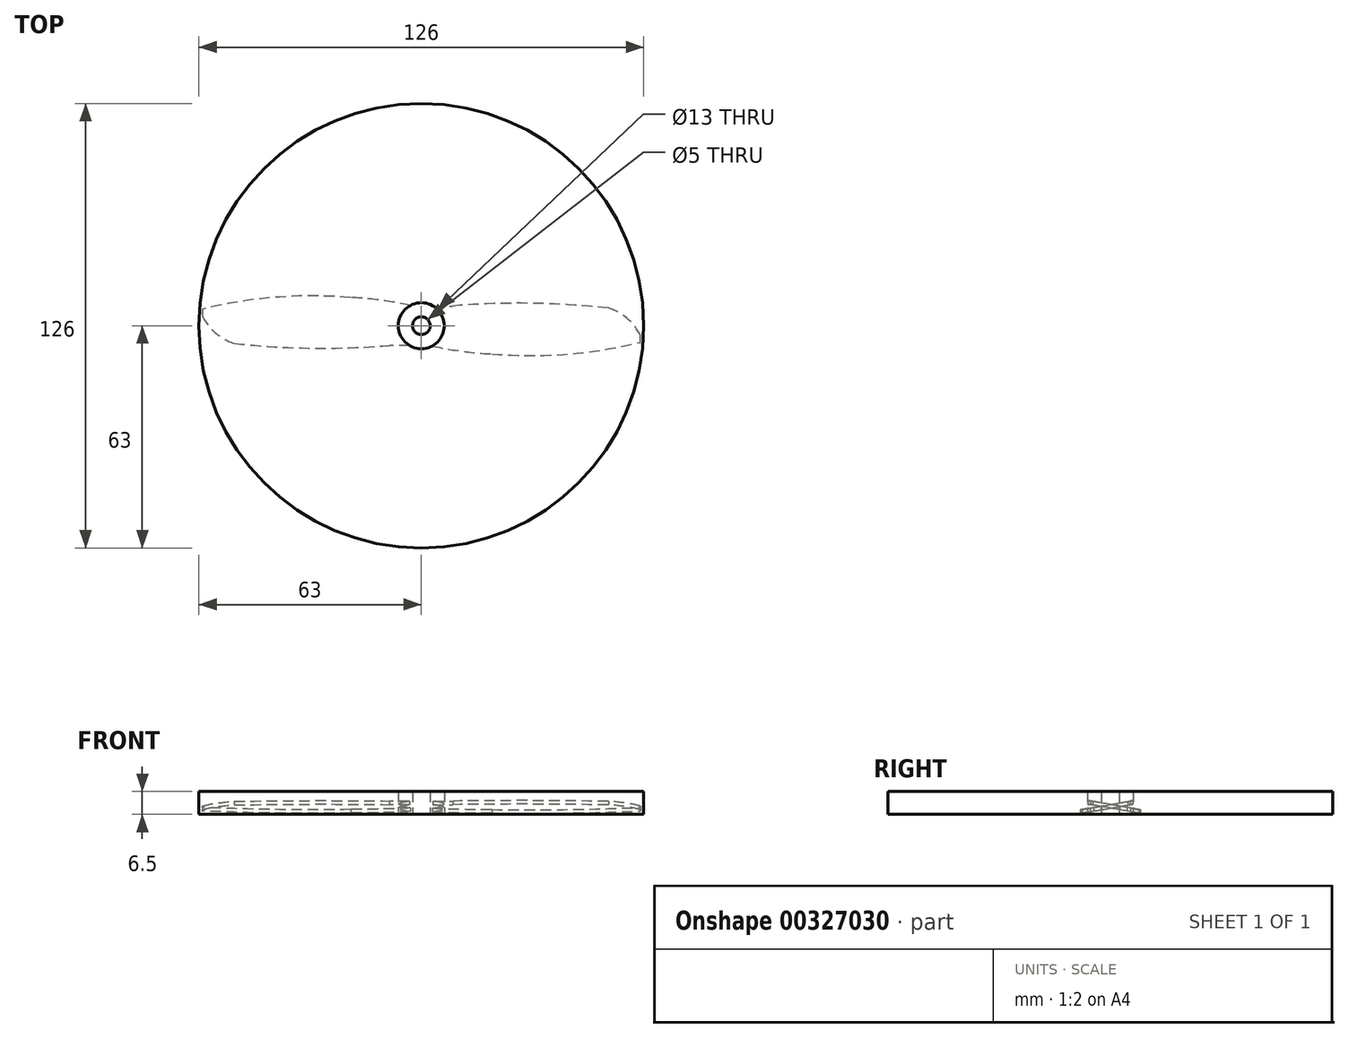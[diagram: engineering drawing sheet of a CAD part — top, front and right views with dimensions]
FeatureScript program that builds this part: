
annotation { "Feature Type Name" : "Feature", "Feature Type Description" : "" }
export const myFeature = defineFeature(function(context is Context, id is Id, definition is map)
    precondition{}
    {
        {
            var Q0;
            Q0=qCreatedBy(makeId("Top.planeOp"),FACE);
            var sketch = newSketch(context, id + "F0", { "sketchPlane" : qUnion([Q0])});
            skCircle(sketch, "E0", {"center": v(0, 0) * mm, "radius": 2.5 * mm});
            skCircle(sketch, "E1", {"center": v(0, 0) * mm, "radius": 6.5 * mm});
            skCircle(sketch, "E2", {"center": v(0, 0) * mm, "radius": 63 * mm});
            skSolve(sketch);
        }
        {
            var Q0;
            Q0=makeQuery(id+"F0.imprint","IMPRINT",FACE,{"disambiguationData":[TD([[makeQuery(id+"F0.imprint","IMPRINT",EDGE,{"derivedFrom":sQuery(id+"F0.wireOp",EDGE,"E0")}),-1.0]])]});
            extrude(context, id + "F1", {"entities" : qUnion([Q0]), "depth" : 6.5 * mm});
        }
        {
            var Q0;
            Q0=qCreatedBy(makeId("Top.planeOp"),FACE);
            var sketch = newSketch(context, id + "F2", { "sketchPlane" : qUnion([Q0])});
            skLineSegment(sketch, "E3.bottom", {"start": v(0, -8) * mm, "end": v(62, -8) * mm});
            skLineSegment(sketch, "E3.top", {"start": v(0, 5.6) * mm, "end": v(62, 5.6) * mm});
            skLineSegment(sketch, "E3.left", {"start": v(0, -8) * mm, "end": v(0, 5.6) * mm});
            skLineSegment(sketch, "E3.right", {"start": v(62, -8) * mm, "end": v(62, 5.6) * mm});
            skPoint(sketch, "E3.middle", {"position": v(31, -1.2) * mm});
            skArc(sketch, "E4", {"start": v(62, -2.7) * mm, "mid": v(55.8, 3.8) * mm, "end": v(47, 5.6) * mm});
            skArc(sketch, "E5", {"start": v(20, -8) * mm, "mid": v(41.13, -8.06) * mm, "end": v(62, -4.7) * mm});
            skArc(sketch, "E6", {"start": v(0, -5) * mm, "mid": v(9.92, -7) * mm, "end": v(20, -8) * mm});
            skArc(sketch, "E7", {"start": v(53, 5) * mm, "mid": v(31.01, 6.36) * mm, "end": v(9, 5.6) * mm});
            skSolve(sketch);
        }
        {
            var Q0;
            {var subQ3=sQuery(id+"F2.wireOp",EDGE,"E6");Q0=makeQuery(id+"F2.imprint","IMPRINT",FACE,{"disambiguationData":[TD([[makeQuery(id+"F2.imprint","IMPRINT",EDGE,{"derivedFrom":subQ3}),1.0]])]});}
            var Q1;
            {var subQ0=sQuery(id+"F2.wireOp",EDGE,"E7");var subQ1=sQuery(id+"F2.wireOp",EDGE,"E3.top");var subQ2=makeQuery(id+"F2.imprint","INTERSECT",VERTEX,{"disambiguationData":[OD(0.0)],"derivedFrom":[subQ1,subQ0]});Q1=makeQuery(id+"F2.imprint","IMPRINT",FACE,{"disambiguationData":[TD([[makeQuery(id+"F2.imprint","IMPRINT",EDGE,{"disambiguationData":[TD([[subQ2,-1.0]])],"derivedFrom":subQ1}),1.0]])]});}
            var Q2;
            {var subQ0=sQuery(id+"F2.wireOp",EDGE,"E5");var subQ1=sQuery(id+"F2.wireOp",EDGE,"E3.bottom");var subQ3=makeQuery(id+"F2.imprint","INTERSECT",VERTEX,{"derivedFrom":[subQ1,subQ0]});Q2=makeQuery(id+"F2.imprint","IMPRINT",FACE,{"disambiguationData":[TD([[makeQuery(id+"F2.imprint","IMPRINT",EDGE,{"disambiguationData":[TD([[subQ3,1.0]])],"derivedFrom":subQ1}),-1.0]])]});}
            extrude(context, id + "F3", {"entities" : qUnion([Q0, Q1, Q2]), "operationType" : NewBodyOperationType.ADD, "depth" : 4.5 * mm});
        }
        {
            var Q0;
            Q0=qCreatedBy(makeId("Right.planeOp"),FACE);
            var sketch = newSketch(context, id + "F4", { "sketchPlane" : qUnion([Q0])});
            skLineSegment(sketch, "E8", {"start": v(-10, 1.02) * mm, "end": v(10, 4.54) * mm});
            skLineSegment(sketch, "E9", {"start": v(10, 4.54) * mm, "end": v(10, 6.02) * mm});
            skLineSegment(sketch, "E10", {"start": v(10, 6.02) * mm, "end": v(-10, 6.02) * mm});
            skLineSegment(sketch, "E11", {"start": v(-10, 6.02) * mm, "end": v(-10, 1.02) * mm});
            skLineSegment(sketch, "E12", {"start": v(-10, 0) * mm, "end": v(10, 3.53) * mm});
            skLineSegment(sketch, "E13", {"start": v(10, 3.53) * mm, "end": v(10, -5) * mm});
            skLineSegment(sketch, "E14", {"start": v(10, -5) * mm, "end": v(-10, -5) * mm});
            skLineSegment(sketch, "E15", {"start": v(-10, -5) * mm, "end": v(-10, 0) * mm});
            skSolve(sketch);
        }
        {
            var Q0;
            Q0 = qSketchRegion(id + "F4", true);
            extrude(context, id + "F5", {"entities" : qUnion([Q0]), "operationType" : NewBodyOperationType.REMOVE, "endBound" : BoundingType.THROUGH_ALL, "depth" : 25 * mm});
        }
        {
            var Q0;
            Q0=qCreatedBy(makeId("Right.planeOp"),FACE);
            var sketch = newSketch(context, id + "F6", { "sketchPlane" : qUnion([Q0])});
            skLineSegment(sketch, "E16", {"start": v(0, 15) * mm, "end": v(0, -15) * mm, "construction": true});
            skSolve(sketch);
        }
        {
            var Q0;
            Q0=makeQuery(id+"F1.opExtrude","SWEPT_BODY",BODY,{"disambiguationData":[OSD([sQuery(id+"F0.wireOp",EDGE,"E0"),sQuery(id+"F0.wireOp",EDGE,"E1")])]});
            var Q1;
            Q1=sQuery(id+"F6.wireOp",EDGE,"E16");
            circularPattern(context, id + "F7", {"operationType" : NewBodyOperationType.ADD, "entities" : qUnion([Q0]), "axis" : qUnion([Q1]), "angle" : 360 * degree, "instanceCount" : 2, "equalSpace" : true});
        }
        {
            var Q0;
            Q0=makeQuery(id+"F0.imprint","IMPRINT",FACE,{"disambiguationData":[TD([[makeQuery(id+"F0.imprint","IMPRINT",EDGE,{"derivedFrom":sQuery(id+"F0.wireOp",EDGE,"E0")}),1.0]])]});
            extrude(context, id + "F8", {"entities" : qUnion([Q0]), "operationType" : NewBodyOperationType.REMOVE, "depth" : 25 * mm});
        }
        {
            var Q0;
            Q0=makeQuery(id+"F0.imprint","IMPRINT",FACE,{"disambiguationData":[TD([[makeQuery(id+"F0.imprint","IMPRINT",EDGE,{"derivedFrom":sQuery(id+"F0.wireOp",EDGE,"E1")}),-1.0]])]});
            extrude(context, id + "F9", {"entities" : qUnion([Q0]), "depth" : 6.5 * mm});
        }
    });
